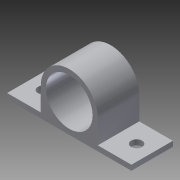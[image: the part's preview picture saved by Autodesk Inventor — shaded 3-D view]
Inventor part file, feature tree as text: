
AUTODESK INVENTOR PART (.ipt)
format: ipt  version: 2013 (Build 170138000, 138)  size: 139,776 bytes
history: native  units: in
note: dims shown in document units (in); Inventor stores cm internally (conversion verified against a paired STEP export)
features: extrude x3, sketch x2
ambient origin geometry x8: Origin, YZ Plane, XZ Plane, XY Plane, X Axis, Y Axis, Z Axis, Center Point
bodies: Solid1 (feature_tree)
feature tree (5):
  extrude  "Extrusion1"  Depth=1.5in
  extrude  "Extrusion2"  Depth=0.6875in
  extrude  "Extrusion3"  Depth=1.125in
  sketch  "Sketch2"  dims[d0=1.5in d1=1.5in]
  sketch  "Sketch3"  dims[d2=0.125in d3=0.6875in d4=1.125in d6=1.0in d7=0.0in d8=0.266in d11=1.0in d12=0.0in d13=0.375in d14=0.266in d15=0.375in d16=0.125in d17=1.0in d18=0.0in]
